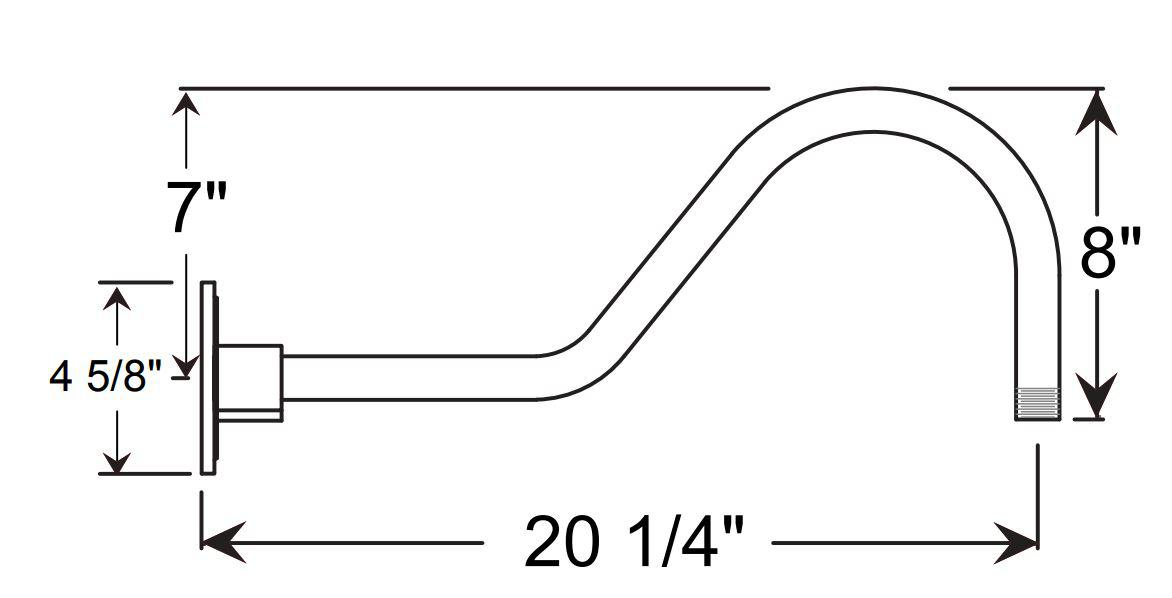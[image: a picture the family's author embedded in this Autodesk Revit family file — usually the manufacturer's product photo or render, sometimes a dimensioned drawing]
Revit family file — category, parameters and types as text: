
# Revit family: VEC 12,16,20,24
name_source: partatom
category: Lighting Fixtures
units: mm (PartAtom-declared; Revit-internal decimal feet)

## family parameters
Always vertical = Yes
Cut with Voids When Loaded = No
Light Source = Yes
OmniClass Number = 23.80.70.00
OmniClass Title = Lighting
Part Type = Normal
Room Calculation Point = No
Round Connector Dimension = Use Diameter
Shared = No
Work Plane-Based = No

## types (4) — shared parameters
Apparent Load = 16 VA
Body Colour = Spun aluminium
Body Material = body
Bulb = Bulb
CRI = >90
Canopy Body = body
Color Filter = 16777215
Construction Material = Heavy Duty spun aluminum.
Default Elevation = 0' - 0"
Description = 120-277 Voltage
Dimming = 1%
Dimming Lamp Color Temperature Shift = <None>
Efficiency = 71-108 lumens per watt
HUB = Steel, Paint Finish, Dark Gray, Matte
Lamp = LED
Life = L70 50,000 hours
Load Classification = Lighting
Manufacturer = ANP Lighting
Power Factor = 1
Tilt Angle = 90.00°
URL = https://www.anplighting.com
Voltage = 220 V
Warranty = 5 year limited warranty
Wattage Comments = 16W
b = 0' - 0"

## per-type parameters (varying)
| type | Fixture Diameter | Fixture Height | Photometric Web File | VEC12 | VEC16 | VEC20 | VEC24 | Weight | a |
| VEC12 | 1' - 0" | 0' - 6 1/4" | VEC12M016LDDW40K.ies | Yes | No | No | No | 2.0lb | 0' - 6" |
| VEC16 | 1' - 4" | 0' - 8 1/2" | VEC16M016LDDW40K.ies | No | Yes | No | No | 3.0lb | 0' - 6" |
| VEC20 | 1' - 8" | 0' - 10 1/2" | VEC20M016LDDW40K.ies | No | No | Yes | No | 6.0lb | 0' - 7 1/2" |
| VEC24 | 2' - 0" | 1' - 0 3/4" | VEC24M016LDDW40K.ies | No | No | No | Yes | 6.0lb | 0' - 8 1/2" |

note: column(s) folded — value = type name in every type: Model

## geometry (parser evidence)
native form markers: Sweep x30
no freeform markers — native parametric forms only
